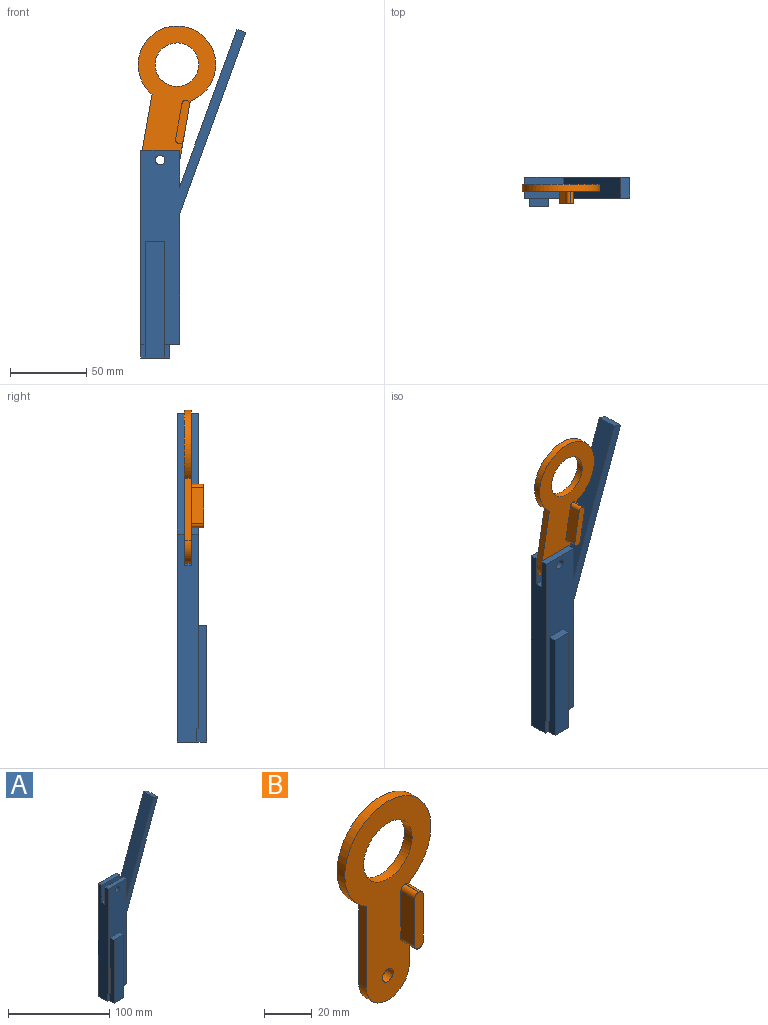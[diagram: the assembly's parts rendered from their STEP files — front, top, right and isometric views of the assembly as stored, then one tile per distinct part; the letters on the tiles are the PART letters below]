
ASSEMBLY  parts=2 mates=1
PART A: 25 faces, bbox 68.8x19.1x215.4 mm
  f0: plane 2.79x1.02mm, normal (0,0,-1), area 2.8mm2, adj f2,f5,f17,f18
  f1: plane 13.72x9.91mm, normal (0,0,-1), area 90.7mm2, adj f2,f8,f11,f20,f21,f22
  f2: plane 206.36x68.84mm, normal (0,-1,0), area 3069.4mm2, adj f0,f1,f3,f5,f7,f8,f9,f10
  f3: plane 24.12x13.72mm, normal (1,0,0), area 237.9mm2, adj f2,f4,f7,f11,f12,f13,f14,f16
  f4: plane 25.4x4.57mm, normal (0,0,1), area 116.1mm2, adj f3,f5,f11,f13
  f5: plane 136.04x13.72mm, normal (-1,0,0), area 1763.8mm2, adj f0,f2,f4,f11,f12,f13,f14,f16
  f6: cylinder r=3.17mm len=6.35mm, axis (0,1,0), area 91.2mm2, adj f11,f13
  f7: plane 103.48x37.66mm, normal (-0.94,0,0.34), area 1510.4mm2, adj f2,f3,f10,f11
  f8: plane 84.92x13.72mm, normal (1,0,0), area 1164.8mm2, adj f1,f2,f9,f11
  f9: plane 119.34x43.44mm, normal (0.94,0,-0.34), area 1741.9mm2, adj f2,f8,f10,f11
  f10: plane 13.72x5.77mm, normal (0.34,0,0.94), area 84.3mm2, adj f2,f7,f9,f11
  f11: plane 215.4x68.84mm, normal (0,1,0), area 4094.6mm2, adj f1,f3,f4,f5,f6,f7,f8,f9
  f12: plane 25.4x4.57mm, normal (0,0,1), area 116.1mm2, adj f3,f5,f13,f16
  f13: plane 25.4x20.32mm, normal (0,-1,0), area 484.5mm2, adj f3,f4,f5,f6,f12
  f14: plane 25.4x4.57mm, normal (0,0,1), area 116.1mm2, adj f2,f3,f5,f16
  f15: cylinder r=3.17mm len=6.35mm, axis (0,1,0), area 91.2mm2, adj f2,f16
  f16: plane 25.4x20.32mm, normal (0,1,0), area 484.5mm2, adj f3,f5,f12,f14,f15
  f17: plane 9.04x2.79mm, normal (0,-1,0), area 25.2mm2, adj f0,f5,f18,f23
  f18: plane 76.2x6.35mm, normal (-1,0,0), area 415.6mm2, adj f0,f2,f17,f19,f23,f24
  f19: plane 76.2x12.7mm, normal (0,-1,0), area 967.7mm2, adj f18,f20,f23,f24
  f20: plane 76.2x6.35mm, normal (1,0,0), area 415.6mm2, adj f1,f2,f19,f21,f23,f24
  f21: plane 9.04x3.56mm, normal (0,-1,0), area 32.1mm2, adj f1,f20,f22,f23
  f22: plane 12.7x9.04mm, normal (1,0,0), area 114.8mm2, adj f1,f11,f21,f23
  f23: plane 19.05x19.05mm, normal (0,0,-1), area 322.6mm2, adj f5,f11,f17,f18,f19,f20,f21,f22
  f24: plane 12.7x5.33mm, normal (0,0,1), area 67.7mm2, adj f2,f18,f19,f20
PART B: 16 faces, bbox 50.8x12.7x101.6 mm
  f0: plane 23.9x8.13mm, normal (-1,0,0), area 194.2mm2, adj f7,f10,f13,f15
  f1: cylinder r=12.7mm len=25.4mm, axis (0,1,0), area 182.4mm2, adj f2,f4,f7,f8
  f2: plane 41.5x12.7mm, normal (1,0,0), area 384mm2, adj f1,f3,f7,f8,f10,f12,f14
  f3: cylinder r=25.4mm len=50.8mm, axis (0,1,0), area 608mm2, adj f2,f4,f7,f8
  f4: plane 41.5x4.57mm, normal (-1,0,0), area 189.8mm2, adj f1,f3,f7,f8
  f5: cylinder r=3.17mm len=6.35mm, axis (0,1,0), area 91.2mm2, adj f7,f8
  f6: cylinder r=14.29mm len=28.58mm, axis (0,1,0), area 410.4mm2, adj f7,f8
  f7: plane 101.6x50.8mm, normal (0,-1,0), area 2461.8mm2, adj f0,f1,f2,f3,f4,f5,f6,f9
  f8: plane 101.6x50.8mm, normal (0,1,0), area 2602.9mm2, adj f1,f2,f3,f4,f5,f6
  f9: plane 8.13x0.17mm, normal (0,0,1), area 1.4mm2, adj f7,f10,f14,f15
  f10: plane 28.8x5.08mm, normal (0,-1,0), area 141.2mm2, adj f0,f2,f9,f11,f12,f13,f14,f15
  f11: plane 8.13x0.17mm, normal (0,0,-1), area 1.4mm2, adj f7,f10,f12,f13
  f12: cylinder r=2.45mm len=8.13mm, axis (0,-1,0), area 31.3mm2, adj f2,f7,f10,f11
  f13: cylinder r=2.45mm len=8.13mm, axis (0,-1,0), area 31.3mm2, adj f0,f7,f10,f11
  f14: cylinder r=2.45mm len=8.13mm, axis (0,1,0), area 31.3mm2, adj f2,f7,f9,f10
  f15: cylinder r=2.45mm len=8.13mm, axis (0,1,0), area 31.3mm2, adj f0,f7,f9,f10
PLACE A t=(13.69,46.45,21.29)mm fixed
PLACE B rot(axis=(0,1,0),10deg) t=(30.8,41.88,99.79)mm
MATE revolute B.f5 <-> A.f6  axis (0,1,0) through (26.39,41.88,74.77)mm
